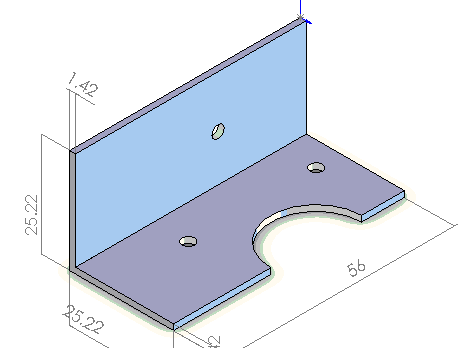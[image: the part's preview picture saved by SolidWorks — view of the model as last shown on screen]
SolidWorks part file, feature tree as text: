
SOLIDWORKS PART (.sldprt)
format: sldprt  version: not decoded by parser v0  size: 131,584 bytes
history: native  units: mm
features: sketch x5, cut_extrude x4, material x1, extrude x1 + 1 further entry (+14 scaffold rows collapsed)
feature tree (26):
  scaffold x14  (default folders/planes/origin — collapsed)
  material  "Material <not specified>"
  "Annotations"  RD1=25.22mm RD2=25.22mm RD3=1.42mm RD4=1.42mm RD5=56mm
  sketch  "Sketch1"
  extrude  "Extrude1"  Depth=56mm
  sketch  "Sketch2"  dims[D1=~4.490128mm]
  cut_extrude  "Cut-Extrude1"  [1 undecoded]
  sketch  "Sketch3"  dims[D1=~11.339659mm]
  cut_extrude  "Cut-Extrude2"  [1 undecoded]
  sketch  "Sketch4"  dims[D1=1.5875mm]
  cut_extrude  "Cut-Extrude3"  [1 undecoded]
  sketch  "Sketch5"  dims[D1=~2.245064mm]
  cut_extrude  "Cut-Extrude4"  [1 undecoded]
decode coverage: 5 of 10 modeling features carry decoded parameters; 1 rows unclassified (native names shown)
note: ~ marks probable driven/reference dimensions
note: 4 parameter values undecoded
summary: no parameter record found for 4 features
note: suppression state not decoded; provenance and decode notes live in map.json
